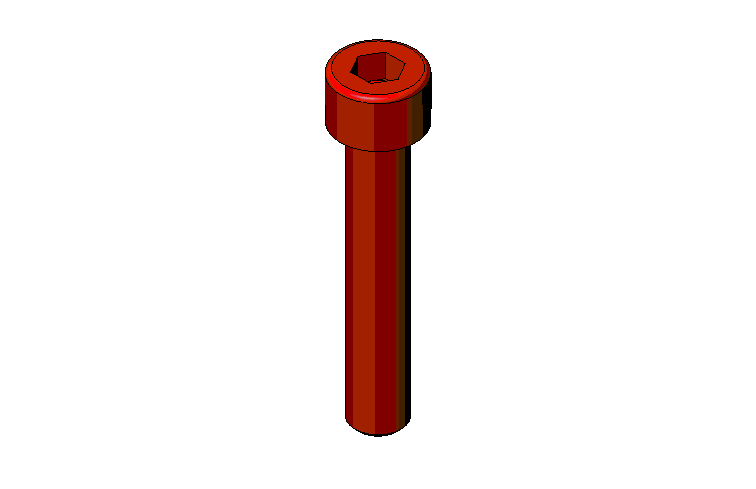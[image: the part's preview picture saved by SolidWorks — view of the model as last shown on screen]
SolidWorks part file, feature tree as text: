
SOLIDWORKS PART (.sldprt)
format: sldprt  version: not decoded by parser v0  size: 181,248 bytes
history: native  units: mm
features: plane x3, sketch x3, material x1, extrude x1, chamfer x1, revolve x1, cut_extrude x1 (+10 scaffold rows collapsed)
feature tree (21):
  scaffold x10  (default folders/planes/origin — collapsed)
  material  "Matériau <non spécifié>"
  plane  "Plan1"
  plane  "Plan2"
  plane  "Plan3"
  sketch  "Esquisse2"  dims[Diamètre nominal=8.0mm]
  extrude  "Base-Extrusion"  Depth=45mm Longueur sous tête=45mm
  chamfer  "Chanfrein1"  Distance=0.8mm Angle=45deg
  sketch  "Esquisse5"  dims[c1.D2=0.8mm c1.Hauteur tête=2.0mm c1.Cote sur plats=5.5mm c1.D3=~2.780036mm c2.D3=30.0deg c2.D4=2.75mm c2.Diamètre tête=13.0mm c2.Diamètre nominal=3.0mm c2.D1=6.5mm c3.D3=3.0mm c4.D3=60.0deg c4.Diamètre nominal=8.0mm c4.Cote sur plats=6.0mm c4.D4=4.0mm c4.D5=3.0mm]
  revolve  "Boss.-Révol.1"  Angle=360deg
  sketch  "Esquisse7"  dims[c1.D1=~2.410714mm c2.D1=30.0deg c2.D2=~1.370242mm c3.D2=30.0deg c3.D3=2.5mm]
  cut_extrude  "Enlèv. mat.-Extru.1"  Depth=4mm
decode coverage: 7 of 7 modeling features carry decoded parameters
note: ~ marks probable driven/reference dimensions
note: suppression state not decoded; provenance and decode notes live in map.json
